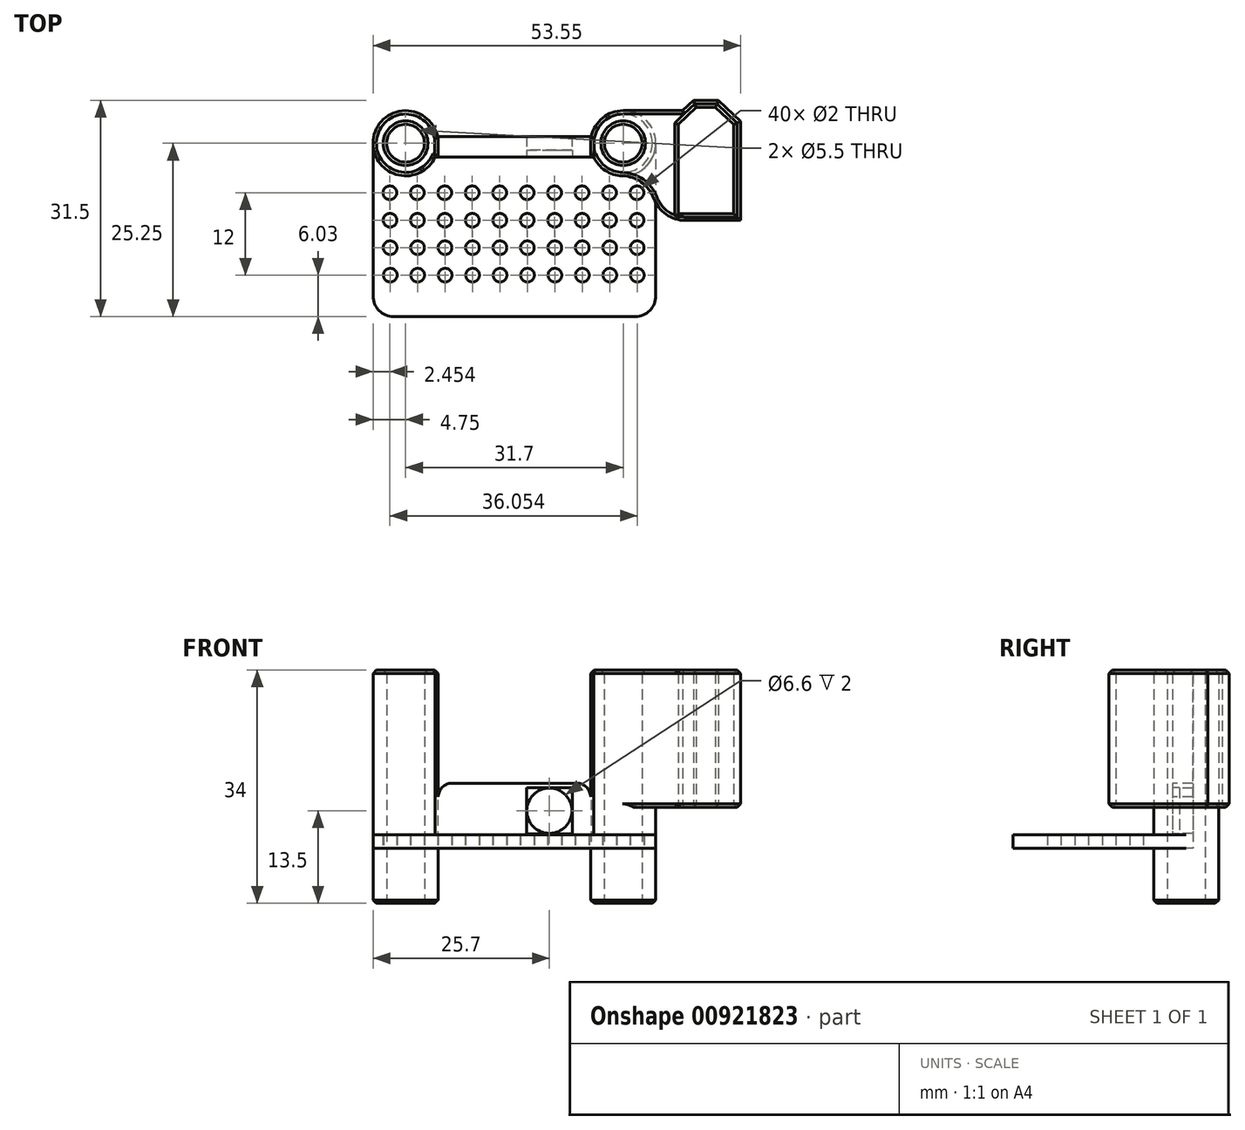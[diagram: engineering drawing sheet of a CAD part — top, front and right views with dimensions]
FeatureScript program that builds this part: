
annotation { "Feature Type Name" : "Feature", "Feature Type Description" : "" }
export const myFeature = defineFeature(function(context is Context, id is Id, definition is map)
    precondition{}
    {
        {
            var Q0;
            Q0=qCreatedBy(makeId("Top.planeOp"),FACE);
            var sketch = newSketch(context, id + "F0", { "sketchPlane" : qUnion([Q0])});
            skLineSegment(sketch, "E0.bottom", {"start": v(15.85, 15) * mm, "end": v(-15.85, 15) * mm});
            skLineSegment(sketch, "E0.top", {"start": v(17.6, -15) * mm, "end": v(-17.6, -15) * mm});
            skLineSegment(sketch, "E0.left", {"start": v(20.6, 10.25) * mm, "end": v(20.6, -12) * mm});
            skLineSegment(sketch, "E0.right", {"start": v(-20.6, 10.25) * mm, "end": v(-20.6, -12) * mm});
            skPoint(sketch, "E0.middle", {"position": v(0, 0) * mm});
            skCircle(sketch, "E1", {"center": v(-15.85, 10.25) * mm, "radius": 2.75 * mm});
            skLineSegment(sketch, "E2", {"start": v(-15.85, 10.25) * mm, "end": v(15.85, 10.25) * mm, "construction": true});
            skCircle(sketch, "E3", {"center": v(15.85, 10.25) * mm, "radius": 2.75 * mm});
            skPoint(sketch, "E4.visualSharp", {"position": v(-20.6, 15) * mm});
            skPoint(sketch, "E5.visualSharp", {"position": v(20.6, 15) * mm});
            skPoint(sketch, "E6.visualSharp", {"position": v(20.6, -15) * mm});
            skArc(sketch, "E6.filletArc", {"start": v(17.6, -15) * mm, "mid": v(19.72, -14.12) * mm, "end": v(20.6, -12) * mm});
            skPoint(sketch, "E7.visualSharp", {"position": v(-20.6, -15) * mm});
            skArc(sketch, "E7.filletArc", {"start": v(-20.6, -12) * mm, "mid": v(-19.72, -14.12) * mm, "end": v(-17.6, -15) * mm});
            skCircle(sketch, "E8.0", {"center": v(-15.85, 10.25) * mm, "radius": 4.75 * mm});
            skCircle(sketch, "E9.0", {"center": v(15.85, 10.25) * mm, "radius": 4.75 * mm});
            skCircle(sketch, "E10", {"center": v(-18.15, 3.03) * mm, "radius": 1 * mm});
            skCircle(sketch, "E11.1.0.0", {"center": v(-14.15, 3.03) * mm, "radius": 1 * mm});
            skCircle(sketch, "E11.2.0.0", {"center": v(-10.15, 3.03) * mm, "radius": 1 * mm});
            skCircle(sketch, "E11.3.0.0", {"center": v(-6.15, 3.03) * mm, "radius": 1 * mm});
            skCircle(sketch, "E11.4.0.0", {"center": v(-2.15, 3.03) * mm, "radius": 1 * mm});
            skCircle(sketch, "E11.5.0.0", {"center": v(1.85, 3.03) * mm, "radius": 1 * mm});
            skCircle(sketch, "E11.6.0.0", {"center": v(5.85, 3.03) * mm, "radius": 1 * mm});
            skCircle(sketch, "E11.7.0.0", {"center": v(9.85, 3.03) * mm, "radius": 1 * mm});
            skCircle(sketch, "E11.8.0.0", {"center": v(13.85, 3.03) * mm, "radius": 1 * mm});
            skCircle(sketch, "E11.9.0.0", {"center": v(17.85, 3.03) * mm, "radius": 1 * mm});
            skLineSegment(sketch, "E11.direction1", {"start": v(-18.15, 3.03) * mm, "end": v(-14.15, 3.03) * mm, "construction": true});
            skCircle(sketch, "E12.1.0.0", {"center": v(-18.12, -0.97) * mm, "radius": 1 * mm});
            skCircle(sketch, "E12.2.0.0", {"center": v(-18.1, -4.97) * mm, "radius": 1 * mm});
            skCircle(sketch, "E12.3.0.0", {"center": v(-18.08, -8.97) * mm, "radius": 1 * mm});
            skLineSegment(sketch, "E12.direction1", {"start": v(-18.15, 3.03) * mm, "end": v(-18.12, -0.97) * mm, "construction": true});
            skCircle(sketch, "E13.1.0.0", {"center": v(-14.13, -0.97) * mm, "radius": 1 * mm});
            skCircle(sketch, "E13.1.0.1", {"center": v(-10.13, -0.97) * mm, "radius": 1 * mm});
            skCircle(sketch, "E13.1.0.2", {"center": v(-6.13, -0.97) * mm, "radius": 1 * mm});
            skCircle(sketch, "E13.1.0.3", {"center": v(-2.13, -0.97) * mm, "radius": 1 * mm});
            skCircle(sketch, "E13.1.0.4", {"center": v(1.87, -0.97) * mm, "radius": 1 * mm});
            skCircle(sketch, "E13.1.0.5", {"center": v(5.87, -0.97) * mm, "radius": 1 * mm});
            skCircle(sketch, "E13.1.0.6", {"center": v(9.87, -0.97) * mm, "radius": 1 * mm});
            skCircle(sketch, "E13.1.0.7", {"center": v(13.87, -0.97) * mm, "radius": 1 * mm});
            skCircle(sketch, "E13.1.0.8", {"center": v(17.87, -0.97) * mm, "radius": 1 * mm});
            skCircle(sketch, "E13.2.0.0", {"center": v(-14.1, -4.97) * mm, "radius": 1 * mm});
            skCircle(sketch, "E13.2.0.1", {"center": v(-10.1, -4.97) * mm, "radius": 1 * mm});
            skCircle(sketch, "E13.2.0.2", {"center": v(-6.1, -4.97) * mm, "radius": 1 * mm});
            skCircle(sketch, "E13.2.0.3", {"center": v(-2.1, -4.97) * mm, "radius": 1 * mm});
            skCircle(sketch, "E13.2.0.4", {"center": v(1.9, -4.97) * mm, "radius": 1 * mm});
            skCircle(sketch, "E13.2.0.5", {"center": v(5.9, -4.97) * mm, "radius": 1 * mm});
            skCircle(sketch, "E13.2.0.6", {"center": v(9.9, -4.97) * mm, "radius": 1 * mm});
            skCircle(sketch, "E13.2.0.7", {"center": v(13.9, -4.97) * mm, "radius": 1 * mm});
            skCircle(sketch, "E13.2.0.8", {"center": v(17.9, -4.97) * mm, "radius": 1 * mm});
            skCircle(sketch, "E13.3.0.0", {"center": v(-14.1, -8.97) * mm, "radius": 1 * mm});
            skCircle(sketch, "E13.3.0.1", {"center": v(-10.1, -8.97) * mm, "radius": 1 * mm});
            skCircle(sketch, "E13.3.0.2", {"center": v(-6.1, -8.97) * mm, "radius": 1 * mm});
            skCircle(sketch, "E13.3.0.3", {"center": v(-2.1, -8.97) * mm, "radius": 1 * mm});
            skCircle(sketch, "E13.3.0.4", {"center": v(1.9, -8.97) * mm, "radius": 1 * mm});
            skCircle(sketch, "E13.3.0.5", {"center": v(5.9, -8.97) * mm, "radius": 1 * mm});
            skCircle(sketch, "E13.3.0.6", {"center": v(9.9, -8.97) * mm, "radius": 1 * mm});
            skCircle(sketch, "E13.3.0.7", {"center": v(13.9, -8.97) * mm, "radius": 1 * mm});
            skCircle(sketch, "E13.3.0.8", {"center": v(17.9, -8.97) * mm, "radius": 1 * mm});
            skLineSegment(sketch, "E13.direction1", {"start": v(-14.15, 3.03) * mm, "end": v(-14.13, -0.97) * mm, "construction": true});
            skSolve(sketch);
        }
        {
            var Q0;
            {var subQ2=sQuery(id+"F0.wireOp",EDGE,"E0.bottom");Q0=makeQuery(id+"F0.imprint","IMPRINT",FACE,{"disambiguationData":[TD([[makeQuery(id+"F0.imprint","IMPRINT",EDGE,{"derivedFrom":subQ2}),1.0]])]});}
            extrude(context, id + "F1", {"entities" : qUnion([Q0]), "depth" : 2 * mm, "offsetDistance" : 25 * mm});
        }
        {
            var Q0;
            Q0=makeQuery(id+"F0.imprint","IMPRINT",FACE,{"disambiguationData":[TD([[makeQuery(id+"F0.imprint","IMPRINT",EDGE,{"derivedFrom":sQuery(id+"F0.wireOp",EDGE,"E1")}),-1.0]])]});
            var Q1;
            Q1=makeQuery(id+"F0.imprint","IMPRINT",FACE,{"disambiguationData":[TD([[makeQuery(id+"F0.imprint","IMPRINT",EDGE,{"derivedFrom":sQuery(id+"F0.wireOp",EDGE,"E3")}),-1.0]])]});
            extrude(context, id + "F2", {"entities" : qUnion([Q0, Q1]), "operationType" : NewBodyOperationType.ADD, "depth" : 26 * mm, "offsetDistance" : 25 * mm, "hasSecondDirection" : true, "secondDirectionOppositeDirection" : true, "secondDirectionDepth" : 8 * mm});
        }
        {
            var Q0;
            {var subQ0=sQuery(id+"F0.wireOp",EDGE,"E6.filletArc");var subQ1=sQuery(id+"F0.wireOp",EDGE,"E0.right");var subQ2=sQuery(id+"F0.wireOp",EDGE,"E0.left");var subQ3=sQuery(id+"F0.wireOp",EDGE,"E0.top");var subQ4=sQuery(id+"F0.wireOp",EDGE,"E7.filletArc");var subQ5=sQuery(id+"F0.wireOp",EDGE,"E8.0");var subQ6=sQuery(id+"F0.wireOp",EDGE,"E9.0");Q0=makeQuery(id+"F9.boolean.opBoolean","SPLIT",FACE,{"disambiguationData":[TD([makeQuery(id+"F1.opExtrude","SWEPT_FACE",FACE,{"disambiguationData":[OSD([subQ3])]})])],"derivedFrom":makeQuery(id+"F1.opExtrude","CAP_FACE",FACE,{"disambiguationData":[OSD([sQuery(id+"F0.wireOp",EDGE,"E0.bottom"),subQ3,subQ2,subQ1,subQ0,subQ4,subQ5,subQ6])],"isStart":false})});}
            cPlane(context, id + "F3", {"entities" : qUnion([Q0]), "cplaneType" : CPlaneType.OFFSET, "offset" : 4 * mm, "width" : 150 * mm, "height" : 150 * mm});
        }
        {
            var Q0;
            Q0=qCreatedBy(id+"F3.planeOp",FACE);
            var sketch = newSketch(context, id + "F4", { "sketchPlane" : qUnion([Q0])});
            skLineSegment(sketch, "E14.bottom", {"start": v(23.85, 0) * mm, "end": v(31.95, 0) * mm});
            skLineSegment(sketch, "E14.top", {"start": v(26.5, 15.5) * mm, "end": v(29.3, 15.5) * mm});
            skLineSegment(sketch, "E14.left", {"start": v(23.85, 0) * mm, "end": v(23.85, 13) * mm});
            skLineSegment(sketch, "E14.right", {"start": v(31.95, 0) * mm, "end": v(31.95, 13) * mm});
            skLineSegment(sketch, "E15", {"start": v(23.85, 13) * mm, "end": v(26.5, 15.5) * mm});
            skLineSegment(sketch, "E16", {"start": v(27.9, 0) * mm, "end": v(27.9, 15.5) * mm, "construction": true});
            skLineSegment(sketch, "E17.MirrorCS", {"start": v(31.95, 13) * mm, "end": v(29.3, 15.5) * mm});
            skLineSegment(sketch, "E18.1", {"start": v(32.95, -1) * mm, "end": v(32.95, 13.42) * mm});
            skLineSegment(sketch, "E18.2", {"start": v(32.95, 13.42) * mm, "end": v(29.7, 16.5) * mm});
            skLineSegment(sketch, "E18.3", {"start": v(20.6, -1) * mm, "end": v(32.95, -1) * mm});
            skLineSegment(sketch, "E18.4", {"start": v(26.1, 16.5) * mm, "end": v(29.7, 16.5) * mm});
            skLineSegment(sketch, "E18.5", {"start": v(24.52, 15) * mm, "end": v(26.1, 16.5) * mm});
            skLineSegment(sketch, "E19.0", {"start": v(24.52, 15) * mm, "end": v(-15.85, 15) * mm});
            skPoint(sketch, "E20.orphan", {"position": v(15.85, 15) * mm});
            skLineSegment(sketch, "E21.0", {"start": v(20.6, 15) * mm, "end": v(20.6, -12) * mm});
            skPoint(sketch, "E22.orphan", {"position": v(20.6, 10.25) * mm});
            skCircle(sketch, "E23.0", {"center": v(15.85, 10.25) * mm, "radius": 2.75 * mm});
            skCircle(sketch, "E24.0", {"center": v(15.85, 10.25) * mm, "radius": 4.75 * mm});
            skLineSegment(sketch, "E25", {"start": v(15.85, 10.25) * mm, "end": v(15.85, 5.5) * mm, "construction": true});
            skLineSegment(sketch, "E26", {"start": v(15.85, 5.5) * mm, "end": v(20.6, 5.5) * mm});
            skSolve(sketch);
        }
        {
            var Q0;
            Q0=makeQuery(id+"F4.imprint","IMPRINT",FACE,{"disambiguationData":[TD([[makeQuery(id+"F4.imprint","IMPRINT",EDGE,{"derivedFrom":sQuery(id+"F4.wireOp",EDGE,"E14.bottom")}),-1.0]])]});
            var Q1;
            {var subQ3=sQuery(id+"F4.wireOp",EDGE,"E26");Q1=makeQuery(id+"F4.imprint","IMPRINT",FACE,{"disambiguationData":[TD([[makeQuery(id+"F4.imprint","IMPRINT",EDGE,{"derivedFrom":subQ3}),1.0]])]});}
            extrude(context, id + "F5", {"entities" : qUnion([Q0, Q1]), "depth" : 20 * mm, "offsetDistance" : 25 * mm});
        }
        {
            var Q0;
            {var subQ0=sQuery(id+"F4.wireOp",EDGE,"E24.0");var subQ1=sQuery(id+"F4.wireOp",EDGE,"E19.0");var subQ2=makeQuery(id+"F4.imprint","INTERSECT",VERTEX,{"derivedFrom":[subQ1,subQ0]});Q0=makeQuery(id+"F4.imprint","IMPRINT",FACE,{"disambiguationData":[TD([[makeQuery(id+"F4.imprint","IMPRINT",EDGE,{"disambiguationData":[TD([[subQ2,1.0]])],"derivedFrom":subQ1}),1.0]])]});}
            extrude(context, id + "F6", {"entities" : qUnion([Q0]), "operationType" : NewBodyOperationType.ADD, "depth" : 20 * mm, "offsetDistance" : 25 * mm});
        }
        {
            var Q0;
            Q0=sQuery(id+"F0.wireOp",EDGE,"E2");
            cPlane(context, id + "F7", {"entities" : qUnion([Q0]), "cplaneType" : CPlaneType.LINE_ANGLE, "offset" : 25 * mm, "angle" : 0 * degree, "width" : 150 * mm, "height" : 150 * mm});
        }
        {
            var Q0;
            Q0=qCreatedBy(id+"F7.planeOp",FACE);
            var sketch = newSketch(context, id + "F8", { "sketchPlane" : qUnion([Q0])});
            skLineSegment(sketch, "E27", {"start": v(-11.1, 26) * mm, "end": v(-11.1, 7.5) * mm});
            skLineSegment(sketch, "E28", {"start": v(11.1, -7.5) * mm, "end": v(11.1, 2) * mm});
            skLineSegment(sketch, "E29.0", {"start": v(-15.85, 2) * mm, "end": v(15.85, 2) * mm});
            skLineSegment(sketch, "E30", {"start": v(-9.1, 9.5) * mm, "end": v(9.1, 9.5) * mm});
            skPoint(sketch, "E31.visualSharp", {"position": v(-11.1, 9.5) * mm});
            skArc(sketch, "E31.filletArc", {"start": v(-9.1, 9.5) * mm, "mid": v(-10.51, 8.91) * mm, "end": v(-11.1, 7.5) * mm});
            skPoint(sketch, "E32.visualSharp", {"position": v(11.1, 9.5) * mm});
            skArc(sketch, "E32.filletArc", {"start": v(11.1, 7.5) * mm, "mid": v(10.51, 8.91) * mm, "end": v(9.1, 9.5) * mm});
            skCircle(sketch, "E33", {"center": v(-5.1, 5.5) * mm, "radius": 3.3 * mm});
            skLineSegment(sketch, "E34.0", {"start": v(-20.6, 26) * mm, "end": v(-11.1, 26) * mm});
            skLineSegment(sketch, "E35", {"start": v(-13.1, 26) * mm, "end": v(-13.1, 2) * mm});
            skLineSegment(sketch, "E36.MirrorCS", {"start": v(13.1, 26) * mm, "end": v(13.1, 2) * mm});
            skLineSegment(sketch, "E37.trimOffspring", {"start": v(-11.1, 2) * mm, "end": v(-11.1, -7.5) * mm});
            skLineSegment(sketch, "E38.0", {"start": v(11.1, 26) * mm, "end": v(20.6, 26) * mm});
            skLineSegment(sketch, "E39.trimOffspring", {"start": v(11.1, 7.5) * mm, "end": v(11.1, 26) * mm});
            skSolve(sketch);
        }
        {
            var Q0;
            Q0=qSketchRegion(id+"F8",true);
            extrude(context, id + "F9", {"entities" : qUnion([Q0]), "operationType" : NewBodyOperationType.ADD, "depth" : 1 * mm, "offsetDistance" : 25 * mm, "hasSecondDirection" : true, "secondDirectionOppositeDirection" : true, "secondDirectionDepth" : 2 * mm});
        }
        {
            var Q0;
            {var subQ0=sQuery(id+"F0.wireOp",EDGE,"E0.bottom");var subQ1=sQuery(id+"F0.wireOp",EDGE,"E8.0");var subQ2=sQuery(id+"F0.wireOp",EDGE,"E9.0");Q0=makeQuery(id+"F9.boolean.opBoolean","SPLIT",FACE,{"disambiguationData":[TD([makeQuery(id+"F1.opExtrude","SWEPT_FACE",FACE,{"disambiguationData":[OSD([subQ0])]})])],"derivedFrom":makeQuery(id+"F1.opExtrude","CAP_FACE",FACE,{"disambiguationData":[OSD([subQ0,sQuery(id+"F0.wireOp",EDGE,"E0.top"),sQuery(id+"F0.wireOp",EDGE,"E0.left"),sQuery(id+"F0.wireOp",EDGE,"E0.right"),sQuery(id+"F0.wireOp",EDGE,"E6.filletArc"),sQuery(id+"F0.wireOp",EDGE,"E7.filletArc"),subQ1,subQ2])],"isStart":false})});}
            var sketch = newSketch(context, id + "F10", { "sketchPlane" : qUnion([Q0])});
            skLineSegment(sketch, "E40.0.0", {"start": v(-11.2, 11.25) * mm, "end": v(11.2, 11.25) * mm});
            skArc(sketch, "E40.0.1", {"start": v(11.2, 11.25) * mm, "mid": v(12.87, 13.95) * mm, "end": v(15.85, 15) * mm});
            skLineSegment(sketch, "E40.0.2", {"start": v(15.85, 15) * mm, "end": v(-15.85, 15) * mm});
            skArc(sketch, "E40.0.3", {"start": v(-15.85, 15) * mm, "mid": v(-12.87, 13.95) * mm, "end": v(-11.2, 11.25) * mm});
            skSolve(sketch);
        }
        {
            var Q0;
            Q0=qSketchRegion(id+"F10",true);
            var Q1;
            Q1=makeQuery(id+"F1.opExtrude","CAP_FACE",FACE,{"disambiguationData":[OSD([sQuery(id+"F0.wireOp",EDGE,"E0.bottom"),sQuery(id+"F0.wireOp",EDGE,"E0.top"),sQuery(id+"F0.wireOp",EDGE,"E0.left"),sQuery(id+"F0.wireOp",EDGE,"E0.right"),sQuery(id+"F0.wireOp",EDGE,"E6.filletArc"),sQuery(id+"F0.wireOp",EDGE,"E7.filletArc"),sQuery(id+"F0.wireOp",EDGE,"E8.0"),sQuery(id+"F0.wireOp",EDGE,"E9.0")])],"isStart":true});
            extrude(context, id + "F11", {"entities" : qUnion([Q0]), "operationType" : NewBodyOperationType.REMOVE, "endBound" : BoundingType.UP_TO_SURFACE, "oppositeDirection" : true, "depth" : 25 * mm, "endBoundEntityFace" : qUnion([Q1]), "offsetDistance" : 25 * mm});
        }
        {
            var Q0;
            Q0=makeQuery(id+"F9.opExtrude","CAP_FACE",FACE,{"disambiguationData":[OSD([sQuery(id+"F8.wireOp",EDGE,"E27"),sQuery(id+"F8.wireOp",EDGE,"E29.0"),sQuery(id+"F8.wireOp",EDGE,"E30"),sQuery(id+"F8.wireOp",EDGE,"E31.filletArc"),sQuery(id+"F8.wireOp",EDGE,"E32.filletArc"),sQuery(id+"F8.wireOp",EDGE,"E33"),sQuery(id+"F8.wireOp",EDGE,"E34.0"),sQuery(id+"F8.wireOp",EDGE,"E35"),sQuery(id+"F8.wireOp",EDGE,"E36.MirrorCS"),sQuery(id+"F8.wireOp",EDGE,"E38.0"),sQuery(id+"F8.wireOp",EDGE,"E39.trimOffspring")])],"isStart":true});
            var sketch = newSketch(context, id + "F12", { "sketchPlane" : qUnion([Q0])});
            skCircle(sketch, "E41.0", {"center": v(5.1, 5.5) * mm, "radius": 3.3 * mm});
            skLineSegment(sketch, "E42.bottom", {"start": v(1.75, 8.85) * mm, "end": v(8.45, 8.85) * mm});
            skLineSegment(sketch, "E42.top", {"start": v(1.75, 2.15) * mm, "end": v(8.45, 2.15) * mm});
            skLineSegment(sketch, "E42.left", {"start": v(1.75, 8.85) * mm, "end": v(1.75, 2.15) * mm});
            skLineSegment(sketch, "E42.right", {"start": v(8.45, 8.85) * mm, "end": v(8.45, 2.15) * mm});
            skSolve(sketch);
        }
        {
            var Q0;
            Q0=makeQuery(id+"F12.imprint","IMPRINT",FACE,{"disambiguationData":[TD([[makeQuery(id+"F12.imprint","IMPRINT",EDGE,{"derivedFrom":sQuery(id+"F12.wireOp",EDGE,"E41.0")}),1.0]])]});
            extrude(context, id + "F13", {"entities" : qUnion([Q0]), "operationType" : NewBodyOperationType.REMOVE, "oppositeDirection" : true, "depth" : 1 * mm, "offsetDistance" : 25 * mm});
        }
        {
            var Q0;
            Q0=makeQuery(id+"F5.opExtrude","SWEPT_EDGE",EDGE,{"disambiguationData":[OSD([sQuery(id+"F4.wireOp",EDGE,"E21.0"),sQuery(id+"F4.wireOp",EDGE,"E26")])]});
            fillet(context, id + "F14", {"entities" : qUnion([Q0]), "radius" : 5 * mm, "tangentPropagation" : true, "allowEdgeOverflow" : false});
        }
        {
            var Q0;
            Q0=makeQuery(id+"F5.opExtrude","SWEPT_EDGE",EDGE,{"disambiguationData":[OSD([sQuery(id+"F4.wireOp",EDGE,"E18.3"),sQuery(id+"F4.wireOp",EDGE,"E21.0")])]});
            fillet(context, id + "F15", {"entities" : qUnion([Q0]), "radius" : 5 * mm, "tangentPropagation" : true, "allowEdgeOverflow" : false});
        }
        {
            var Q0;
            Q0=makeQuery(id+"F5.opExtrude","CAP_EDGE",EDGE,{"disambiguationData":[OSD([sQuery(id+"F4.wireOp",EDGE,"E18.3")])],"isStart":false});
            var Q1;
            Q1=makeQuery(id+"F5.opExtrude","CAP_EDGE",EDGE,{"disambiguationData":[OSD([sQuery(id+"F4.wireOp",EDGE,"E18.1")])],"isStart":false});
            var Q2;
            Q2=makeQuery(id+"F5.opExtrude","CAP_EDGE",EDGE,{"disambiguationData":[OSD([sQuery(id+"F4.wireOp",EDGE,"E18.2")])],"isStart":false});
            var Q3;
            Q3=makeQuery(id+"F5.opExtrude","CAP_EDGE",EDGE,{"disambiguationData":[OSD([sQuery(id+"F4.wireOp",EDGE,"E18.4")])],"isStart":false});
            var Q4;
            Q4=makeQuery(id+"F5.opExtrude","CAP_EDGE",EDGE,{"disambiguationData":[OSD([sQuery(id+"F4.wireOp",EDGE,"E18.5")])],"isStart":false});
            var Q5;
            Q5=makeQuery(id+"F5.opExtrude","CAP_EDGE",EDGE,{"disambiguationData":[OSD([sQuery(id+"F4.wireOp",EDGE,"E19.0")])],"isStart":false});
            var Q6;
            Q6=makeQuery(id+"F6.opExtrude","CAP_EDGE",EDGE,{"disambiguationData":[OSD([sQuery(id+"F4.wireOp",EDGE,"E19.0")])],"isStart":true});
            var Q7;
            Q7=makeQuery(id+"F5.opExtrude","CAP_EDGE",EDGE,{"disambiguationData":[OSD([sQuery(id+"F4.wireOp",EDGE,"E18.3")])],"isStart":true});
            var Q8;
            Q8=makeQuery(id+"F5.opExtrude","CAP_EDGE",EDGE,{"disambiguationData":[OSD([sQuery(id+"F4.wireOp",EDGE,"E18.1")])],"isStart":true});
            var Q9;
            Q9=makeQuery(id+"F5.opExtrude","CAP_EDGE",EDGE,{"disambiguationData":[OSD([sQuery(id+"F4.wireOp",EDGE,"E18.2")])],"isStart":true});
            var Q10;
            Q10=makeQuery(id+"F5.opExtrude","CAP_EDGE",EDGE,{"disambiguationData":[OSD([sQuery(id+"F4.wireOp",EDGE,"E19.0")])],"isStart":true});
            var Q11;
            Q11=makeQuery(id+"F5.opExtrude","CAP_EDGE",EDGE,{"disambiguationData":[OSD([sQuery(id+"F4.wireOp",EDGE,"E18.5")])],"isStart":true});
            var Q12;
            Q12=makeQuery(id+"F5.opExtrude","CAP_EDGE",EDGE,{"disambiguationData":[OSD([sQuery(id+"F4.wireOp",EDGE,"E18.4")])],"isStart":true});
            var Q13;
            Q13=makeQuery(id+"F5.opExtrude","CAP_EDGE",EDGE,{"disambiguationData":[OSD([sQuery(id+"F4.wireOp",EDGE,"E14.left")])],"isStart":true});
            var Q14;
            Q14=makeQuery(id+"F5.opExtrude","CAP_EDGE",EDGE,{"disambiguationData":[OSD([sQuery(id+"F4.wireOp",EDGE,"E15")])],"isStart":true});
            var Q15;
            Q15=makeQuery(id+"F5.opExtrude","CAP_EDGE",EDGE,{"disambiguationData":[OSD([sQuery(id+"F4.wireOp",EDGE,"E14.top")])],"isStart":true});
            var Q16;
            Q16=makeQuery(id+"F5.opExtrude","CAP_EDGE",EDGE,{"disambiguationData":[OSD([sQuery(id+"F4.wireOp",EDGE,"E17.MirrorCS")])],"isStart":true});
            var Q17;
            Q17=makeQuery(id+"F5.opExtrude","CAP_EDGE",EDGE,{"disambiguationData":[OSD([sQuery(id+"F4.wireOp",EDGE,"E14.right")])],"isStart":true});
            var Q18;
            Q18=makeQuery(id+"F5.opExtrude","CAP_EDGE",EDGE,{"disambiguationData":[OSD([sQuery(id+"F4.wireOp",EDGE,"E14.bottom")])],"isStart":true});
            var Q19;
            {var subQ0=sQuery(id+"F4.wireOp",EDGE,"E21.0");var subQ1=sQuery(id+"F4.wireOp",EDGE,"E18.3");Q19=makeQuery(id+"F15.opFillet","BLEND_EDGE",EDGE,{"blendedFrom":[makeQuery(id+"F5.opExtrude","SWEPT_EDGE",EDGE,{"disambiguationData":[OSD([subQ1,subQ0])]}),makeQuery(id+"F5.opExtrude","CAP_FACE",FACE,{"disambiguationData":[OSD([sQuery(id+"F4.wireOp",EDGE,"E14.bottom"),sQuery(id+"F4.wireOp",EDGE,"E14.top"),sQuery(id+"F4.wireOp",EDGE,"E14.left"),sQuery(id+"F4.wireOp",EDGE,"E14.right"),sQuery(id+"F4.wireOp",EDGE,"E15"),sQuery(id+"F4.wireOp",EDGE,"E17.MirrorCS"),sQuery(id+"F4.wireOp",EDGE,"E18.1"),sQuery(id+"F4.wireOp",EDGE,"E18.2"),subQ1,sQuery(id+"F4.wireOp",EDGE,"E18.4"),sQuery(id+"F4.wireOp",EDGE,"E18.5"),sQuery(id+"F4.wireOp",EDGE,"E19.0"),subQ0,sQuery(id+"F4.wireOp",EDGE,"E24.0"),sQuery(id+"F4.wireOp",EDGE,"E26")])],"isStart":true})],"blendedInto":[makeQuery(id+"F5.opExtrude","CAP_FACE",FACE,{"disambiguationData":[OSD([sQuery(id+"F4.wireOp",EDGE,"E14.bottom"),sQuery(id+"F4.wireOp",EDGE,"E14.top"),sQuery(id+"F4.wireOp",EDGE,"E14.left"),sQuery(id+"F4.wireOp",EDGE,"E14.right"),sQuery(id+"F4.wireOp",EDGE,"E15"),sQuery(id+"F4.wireOp",EDGE,"E17.MirrorCS"),sQuery(id+"F4.wireOp",EDGE,"E18.1"),sQuery(id+"F4.wireOp",EDGE,"E18.2"),subQ1,sQuery(id+"F4.wireOp",EDGE,"E18.4"),sQuery(id+"F4.wireOp",EDGE,"E18.5"),sQuery(id+"F4.wireOp",EDGE,"E19.0"),subQ0,sQuery(id+"F4.wireOp",EDGE,"E24.0"),sQuery(id+"F4.wireOp",EDGE,"E26")])],"isStart":true})]});}
            var Q20;
            {var subQ0=sQuery(id+"F4.wireOp",EDGE,"E26");var subQ1=sQuery(id+"F4.wireOp",EDGE,"E21.0");Q20=makeQuery(id+"F14.opFillet","BLEND_EDGE",EDGE,{"blendedFrom":[makeQuery(id+"F5.opExtrude","SWEPT_EDGE",EDGE,{"disambiguationData":[OSD([subQ1,subQ0])]}),makeQuery(id+"F5.opExtrude","CAP_FACE",FACE,{"disambiguationData":[OSD([sQuery(id+"F4.wireOp",EDGE,"E14.bottom"),sQuery(id+"F4.wireOp",EDGE,"E14.top"),sQuery(id+"F4.wireOp",EDGE,"E14.left"),sQuery(id+"F4.wireOp",EDGE,"E14.right"),sQuery(id+"F4.wireOp",EDGE,"E15"),sQuery(id+"F4.wireOp",EDGE,"E17.MirrorCS"),sQuery(id+"F4.wireOp",EDGE,"E18.1"),sQuery(id+"F4.wireOp",EDGE,"E18.2"),sQuery(id+"F4.wireOp",EDGE,"E18.3"),sQuery(id+"F4.wireOp",EDGE,"E18.4"),sQuery(id+"F4.wireOp",EDGE,"E18.5"),sQuery(id+"F4.wireOp",EDGE,"E19.0"),subQ1,sQuery(id+"F4.wireOp",EDGE,"E24.0"),subQ0])],"isStart":true})],"blendedInto":[makeQuery(id+"F5.opExtrude","CAP_FACE",FACE,{"disambiguationData":[OSD([sQuery(id+"F4.wireOp",EDGE,"E14.bottom"),sQuery(id+"F4.wireOp",EDGE,"E14.top"),sQuery(id+"F4.wireOp",EDGE,"E14.left"),sQuery(id+"F4.wireOp",EDGE,"E14.right"),sQuery(id+"F4.wireOp",EDGE,"E15"),sQuery(id+"F4.wireOp",EDGE,"E17.MirrorCS"),sQuery(id+"F4.wireOp",EDGE,"E18.1"),sQuery(id+"F4.wireOp",EDGE,"E18.2"),sQuery(id+"F4.wireOp",EDGE,"E18.3"),sQuery(id+"F4.wireOp",EDGE,"E18.4"),sQuery(id+"F4.wireOp",EDGE,"E18.5"),sQuery(id+"F4.wireOp",EDGE,"E19.0"),subQ1,sQuery(id+"F4.wireOp",EDGE,"E24.0"),subQ0])],"isStart":true})]});}
            var Q21;
            {var subQ0=sQuery(id+"F4.wireOp",EDGE,"E21.0");var subQ1=sQuery(id+"F4.wireOp",EDGE,"E18.3");Q21=makeQuery(id+"F15.opFillet","BLEND_EDGE",EDGE,{"blendedFrom":[makeQuery(id+"F5.opExtrude","SWEPT_EDGE",EDGE,{"disambiguationData":[OSD([subQ1,subQ0])]}),makeQuery(id+"F5.opExtrude","CAP_FACE",FACE,{"disambiguationData":[OSD([sQuery(id+"F4.wireOp",EDGE,"E14.bottom"),sQuery(id+"F4.wireOp",EDGE,"E14.top"),sQuery(id+"F4.wireOp",EDGE,"E14.left"),sQuery(id+"F4.wireOp",EDGE,"E14.right"),sQuery(id+"F4.wireOp",EDGE,"E15"),sQuery(id+"F4.wireOp",EDGE,"E17.MirrorCS"),sQuery(id+"F4.wireOp",EDGE,"E18.1"),sQuery(id+"F4.wireOp",EDGE,"E18.2"),subQ1,sQuery(id+"F4.wireOp",EDGE,"E18.4"),sQuery(id+"F4.wireOp",EDGE,"E18.5"),sQuery(id+"F4.wireOp",EDGE,"E19.0"),subQ0,sQuery(id+"F4.wireOp",EDGE,"E24.0"),sQuery(id+"F4.wireOp",EDGE,"E26")])],"isStart":false})],"blendedInto":[makeQuery(id+"F5.opExtrude","CAP_FACE",FACE,{"disambiguationData":[OSD([sQuery(id+"F4.wireOp",EDGE,"E14.bottom"),sQuery(id+"F4.wireOp",EDGE,"E14.top"),sQuery(id+"F4.wireOp",EDGE,"E14.left"),sQuery(id+"F4.wireOp",EDGE,"E14.right"),sQuery(id+"F4.wireOp",EDGE,"E15"),sQuery(id+"F4.wireOp",EDGE,"E17.MirrorCS"),sQuery(id+"F4.wireOp",EDGE,"E18.1"),sQuery(id+"F4.wireOp",EDGE,"E18.2"),subQ1,sQuery(id+"F4.wireOp",EDGE,"E18.4"),sQuery(id+"F4.wireOp",EDGE,"E18.5"),sQuery(id+"F4.wireOp",EDGE,"E19.0"),subQ0,sQuery(id+"F4.wireOp",EDGE,"E24.0"),sQuery(id+"F4.wireOp",EDGE,"E26")])],"isStart":false})]});}
            var Q22;
            {var subQ0=sQuery(id+"F4.wireOp",EDGE,"E26");var subQ1=sQuery(id+"F4.wireOp",EDGE,"E21.0");Q22=makeQuery(id+"F14.opFillet","BLEND_EDGE",EDGE,{"blendedFrom":[makeQuery(id+"F5.opExtrude","SWEPT_EDGE",EDGE,{"disambiguationData":[OSD([subQ1,subQ0])]}),makeQuery(id+"F5.opExtrude","CAP_FACE",FACE,{"disambiguationData":[OSD([sQuery(id+"F4.wireOp",EDGE,"E14.bottom"),sQuery(id+"F4.wireOp",EDGE,"E14.top"),sQuery(id+"F4.wireOp",EDGE,"E14.left"),sQuery(id+"F4.wireOp",EDGE,"E14.right"),sQuery(id+"F4.wireOp",EDGE,"E15"),sQuery(id+"F4.wireOp",EDGE,"E17.MirrorCS"),sQuery(id+"F4.wireOp",EDGE,"E18.1"),sQuery(id+"F4.wireOp",EDGE,"E18.2"),sQuery(id+"F4.wireOp",EDGE,"E18.3"),sQuery(id+"F4.wireOp",EDGE,"E18.4"),sQuery(id+"F4.wireOp",EDGE,"E18.5"),sQuery(id+"F4.wireOp",EDGE,"E19.0"),subQ1,sQuery(id+"F4.wireOp",EDGE,"E24.0"),subQ0])],"isStart":false})],"blendedInto":[makeQuery(id+"F5.opExtrude","CAP_FACE",FACE,{"disambiguationData":[OSD([sQuery(id+"F4.wireOp",EDGE,"E14.bottom"),sQuery(id+"F4.wireOp",EDGE,"E14.top"),sQuery(id+"F4.wireOp",EDGE,"E14.left"),sQuery(id+"F4.wireOp",EDGE,"E14.right"),sQuery(id+"F4.wireOp",EDGE,"E15"),sQuery(id+"F4.wireOp",EDGE,"E17.MirrorCS"),sQuery(id+"F4.wireOp",EDGE,"E18.1"),sQuery(id+"F4.wireOp",EDGE,"E18.2"),sQuery(id+"F4.wireOp",EDGE,"E18.3"),sQuery(id+"F4.wireOp",EDGE,"E18.4"),sQuery(id+"F4.wireOp",EDGE,"E18.5"),sQuery(id+"F4.wireOp",EDGE,"E19.0"),subQ1,sQuery(id+"F4.wireOp",EDGE,"E24.0"),subQ0])],"isStart":false})]});}
            var Q23;
            Q23=makeQuery(id+"F6.opExtrude","CAP_EDGE",EDGE,{"disambiguationData":[OSD([sQuery(id+"F4.wireOp",EDGE,"E19.0")])],"isStart":false});
            var Q24;
            Q24=makeQuery(id+"F9.boolean.opBoolean","MERGE",FACE,{"derivedFrom":[makeQuery(id+"F6.boolean.opBoolean","MERGE",FACE,{"derivedFrom":[makeQuery(id+"F2.opExtrude","CAP_FACE",FACE,{"disambiguationData":[OSD([sQuery(id+"F0.wireOp",EDGE,"E3"),sQuery(id+"F0.wireOp",EDGE,"E9.0")])],"isStart":false}),makeQuery(id+"F6.opExtrude","CAP_FACE",FACE,{"disambiguationData":[OSD([sQuery(id+"F4.wireOp",EDGE,"E19.0"),sQuery(id+"F4.wireOp",EDGE,"E21.0"),sQuery(id+"F4.wireOp",EDGE,"E24.0")])],"isStart":false})]}),makeQuery(id+"F9.opExtrude","SWEPT_FACE",FACE,{"disambiguationData":[OSD([sQuery(id+"F8.wireOp",EDGE,"E34.0")])]})]});
            var Q25;
            Q25=makeQuery(id+"F9.boolean.opBoolean","MERGE",FACE,{"derivedFrom":[makeQuery(id+"F2.opExtrude","CAP_FACE",FACE,{"disambiguationData":[OSD([sQuery(id+"F0.wireOp",EDGE,"E1"),sQuery(id+"F0.wireOp",EDGE,"E8.0")])],"isStart":false}),makeQuery(id+"F9.opExtrude","SWEPT_FACE",FACE,{"disambiguationData":[OSD([sQuery(id+"F8.wireOp",EDGE,"E38.0")])]})]});
            var Q26;
            Q26=makeQuery(id+"F2.opExtrude","CAP_FACE",FACE,{"disambiguationData":[OSD([sQuery(id+"F0.wireOp",EDGE,"E3"),sQuery(id+"F0.wireOp",EDGE,"E9.0")])],"isStart":true});
            var Q27;
            Q27=makeQuery(id+"F2.opExtrude","CAP_FACE",FACE,{"disambiguationData":[OSD([sQuery(id+"F0.wireOp",EDGE,"E1"),sQuery(id+"F0.wireOp",EDGE,"E8.0")])],"isStart":true});
            chamfer(context, id + "F16", {"entities" : qUnion([Q0, Q1, Q2, Q3, Q4, Q5, Q6, Q7, Q8, Q9, Q10, Q11, Q12, Q13, Q14, Q15, Q16, Q17, Q18, Q19, Q20, Q21, Q22, Q23, Q24, Q25, Q26, Q27]), "width" : 0.5 * mm});
        }
    });
